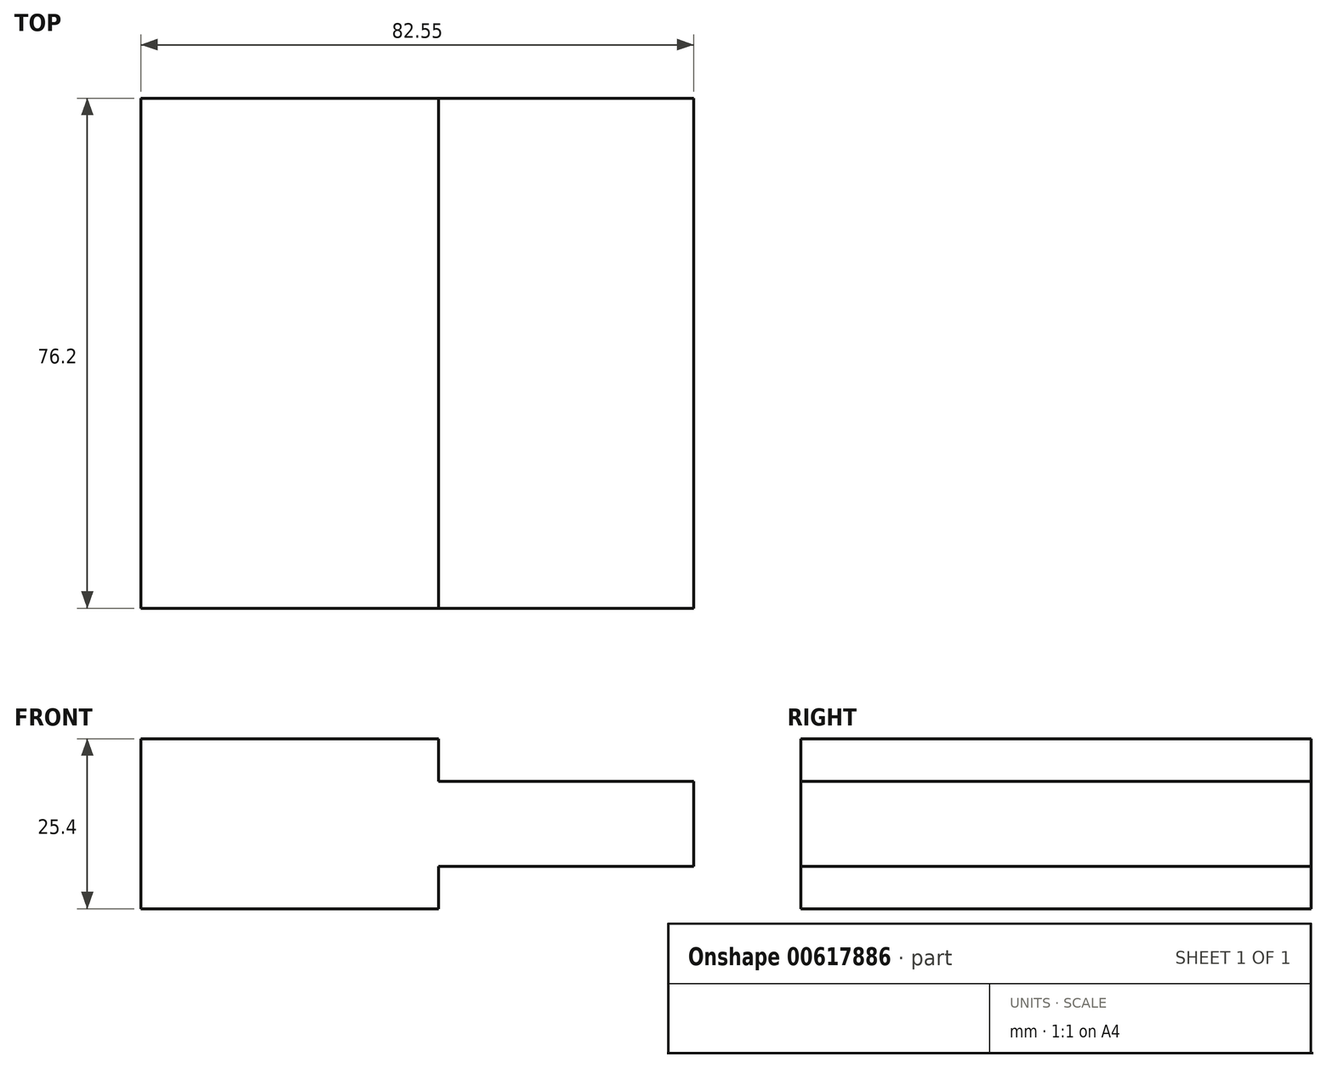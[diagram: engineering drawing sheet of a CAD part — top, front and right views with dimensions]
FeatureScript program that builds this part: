
annotation { "Feature Type Name" : "Feature", "Feature Type Description" : "" }
export const myFeature = defineFeature(function(context is Context, id is Id, definition is map)
    precondition{}
    {
        {
            var Q0;
            Q0=qCreatedBy(makeId("Front.planeOp"),FACE);
            var sketch = newSketch(context, id + "F0", { "sketchPlane" : qUnion([Q0])});
            skLineSegment(sketch, "E0", {"start": v(0, 0) * mm, "end": v(44.45, 0) * mm});
            skLineSegment(sketch, "E1", {"start": v(44.45, 0) * mm, "end": v(44.45, 6.35) * mm});
            skLineSegment(sketch, "E2", {"start": v(44.45, 6.35) * mm, "end": v(82.55, 6.35) * mm});
            skLineSegment(sketch, "E3", {"start": v(82.55, 6.35) * mm, "end": v(82.55, 19.05) * mm});
            skLineSegment(sketch, "E4", {"start": v(82.55, 19.05) * mm, "end": v(44.45, 19.05) * mm});
            skLineSegment(sketch, "E5", {"start": v(44.45, 19.05) * mm, "end": v(44.45, 25.4) * mm});
            skLineSegment(sketch, "E6", {"start": v(44.45, 25.4) * mm, "end": v(0, 25.4) * mm});
            skLineSegment(sketch, "E7", {"start": v(0, 25.4) * mm, "end": v(0, 0) * mm});
            skSolve(sketch);
        }
        {
            var Q0;
            Q0 = qSketchRegion(id + "F0", true);
            extrude(context, id + "F1", {"entities" : qUnion([Q0]), "depth" : 76.2 * mm, "offsetDistance" : 25.4 * mm});
        }
    });
